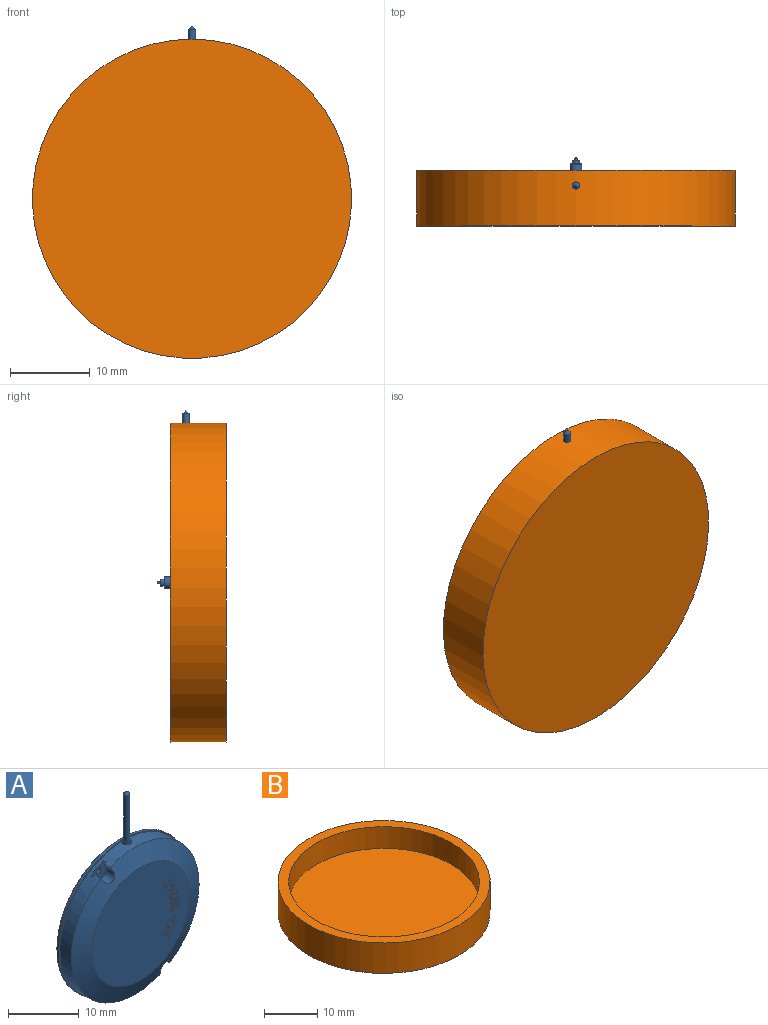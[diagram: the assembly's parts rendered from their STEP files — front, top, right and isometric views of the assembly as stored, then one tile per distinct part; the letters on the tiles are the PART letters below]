
ASSEMBLY  parts=2 mates=1
PART A: 165 faces, bbox 26x6.4x34.7 mm
  f0: cylinder r=0.51mm len=1.05mm, axis (0,-1,0), area 3.4mm2, adj f28,f42,f50
  f1: cylinder r=0.51mm len=1.05mm, axis (0,-1,0), area 3.4mm2, adj f28,f37,f49
  f2: cylinder r=0.4mm len=2.16mm, axis (0,1,0), area 5.1mm2, adj f13,f14,f21,f28,f48
  f3: cylinder r=0.4mm len=2.15mm, axis (0,1,0), area 5.1mm2, adj f13,f14,f21,f28,f47
  f4: cone r=0.45mm half-angle=45deg, axis (0,0,-1), area 0.9mm2, adj f5
  f5: cylinder r=0.45mm len=8.1mm, axis (0,0,-1), area 22.9mm2, adj f4,f35
  f6: cylinder r=0.55mm len=1.1mm, axis (0,0,-1), area 3.8mm2, adj f34,f35
  f7: cylinder r=0.68mm len=1.35mm, axis (0,0,1), area 3.5mm2, adj f15,f19,f27,f34
  f8: cone r=0.72mm half-angle=30deg, axis (0,-1,0), area 0.3mm2, adj f12,f33
  f9: cylinder r=0.45mm len=0.9mm, axis (0,1,0), area 1.1mm2, adj f32,f33
  f10: cylinder r=0.35mm len=0.7mm, axis (0,1,0), area 1.2mm2, adj f31,f32
  f11: cone r=0.13mm half-angle=0.6deg, axis (0,-1,0), area 0.8mm2, adj f30,f31
  f12: cylinder r=0.75mm len=1.5mm, axis (0,1,0), area 4.2mm2, adj f8,f29
  f13: torus R=9mm, axis (0,-1,0), area 224.2mm2, adj f2,f3,f14,f21,f29
  f14: cylinder r=12.57mm len=24.47mm, axis (0,-1,0), area 15.7mm2, adj f2,f3,f13,f28,f50
  f15: cylinder r=13mm len=26mm, axis (0,-1,0), area 32.6mm2, adj f7,f27,f28
  f16: cone r=12.8mm half-angle=70deg, axis (0,1,0), area 219.9mm2, adj f17,f18,f19,f20,f24,f26,f38,f43
  f17: cone r=12.8mm half-angle=70deg, axis (0,1,0), area 0mm2, adj f16,f19,f39
  f18: cylinder r=12.8mm len=1.16mm, axis (0,-1,0), area 0.5mm2, adj f16,f19,f23,f44
  f19: cylinder r=12.8mm len=25.6mm, axis (0,-1,0), area 176mm2, adj f7,f16,f17,f18,f23,f27,f36,f37
  f20: plane 19.6x19.6mm, normal (0,-1,0), area 296.8mm2, adj f16,f51,f52,f53,f54,f55,f56,f57
  f21: cylinder r=12.57mm len=24.47mm, axis (0,-1,0), area 15.7mm2, adj f2,f3,f13,f28,f49
  f22: cylinder r=1.5mm len=2.82mm, axis (0,1,0), area 2.4mm2, adj f23,f42,f45,f46
  f23: plane 3.11x2.74mm, normal (0,1,0), area 2.4mm2, adj f18,f19,f22,f24,f43,f44,f45,f46
  f24: cylinder r=1.05mm len=1.98mm, axis (0,1,0), area 4.6mm2, adj f16,f23,f43,f44
  f25: cylinder r=1.5mm len=2.82mm, axis (0,1,0), area 2.4mm2, adj f36,f37,f40,f41
  f26: cylinder r=1.05mm len=1.98mm, axis (0,1,0), area 5.4mm2, adj f16,f36,f38,f39
  f27: plane 26x26mm, normal (0,-1,0), area 16.1mm2, adj f7,f15,f19
  f28: plane 26x26mm, normal (0,1,0), area 34.5mm2, adj f0,f1,f2,f3,f14,f15,f21
  f29: plane 18.66x18.66mm, normal (0,1,0), area 271.6mm2, adj f12,f13
  f30: plane 0.25x0.25mm, normal (0,1,0), area 0mm2, adj f11
  f31: plane 0.7x0.7mm, normal (0,1,0), area 0.3mm2, adj f10,f11
  f32: plane 0.9x0.9mm, normal (0,1,0), area 0.3mm2, adj f9,f10
  f33: plane 1.43x1.43mm, normal (0,1,0), area 1mm2, adj f8,f9
  f34: plane 1.35x1.35mm, normal (0,0,1), area 0.5mm2, adj f6,f7
  f35: plane 1.1x1.1mm, normal (0,0,1), area 0.3mm2, adj f5,f6
  f36: plane 3.11x2.74mm, normal (0,1,0), area 2.4mm2, adj f19,f25,f26,f38,f39,f40,f41
  f37: plane 3.11x2.74mm, normal (0,-1,0), area 4.7mm2, adj f1,f19,f25,f40,f41
  f38: plane 1.4x0.58mm, normal (0.88,0,0.47), area 0.8mm2, adj f16,f19,f26,f36
  f39: plane 1.4x0.58mm, normal (-0.88,0,-0.47), area 0.8mm2, adj f17,f19,f26,f36
  f40: plane 0.54x0.5mm, normal (-0.88,0,-0.47), area 0.3mm2, adj f19,f25,f36,f37
  f41: plane 0.54x0.5mm, normal (0.88,0,0.47), area 0.3mm2, adj f19,f25,f36,f37
  f42: plane 3.11x2.74mm, normal (0,-1,0), area 4.7mm2, adj f0,f19,f22,f45,f46
  f43: plane 1.4x0.58mm, normal (-0.88,0,-0.47), area 0.8mm2, adj f16,f19,f23,f24
  f44: plane 1.4x0.58mm, normal (0.88,0,0.47), area 0.8mm2, adj f16,f18,f23,f24
  f45: plane 0.54x0.5mm, normal (0.88,0,0.47), area 0.3mm2, adj f19,f22,f23,f42
  f46: plane 0.54x0.5mm, normal (-0.88,0,-0.47), area 0.3mm2, adj f19,f22,f23,f42
  f47: plane 0.8x0.8mm, normal (0,1,0), area 0.5mm2, adj f3
  f48: plane 0.8x0.8mm, normal (0,1,0), area 0.5mm2, adj f2
  f49: plane 1.02x1.02mm, normal (0,-1,0), area 0.8mm2, adj f1,f21
  f50: plane 1.02x1.02mm, normal (0,-1,0), area 0.8mm2, adj f0,f14
  f51: plane 1.15x0.96mm, normal (0.64,0,0.77), area 0.3mm2, adj f20,f52,f62,f63
  f52: plane 0.66x0.55mm, normal (0.77,0,-0.64), area 0.2mm2, adj f20,f51,f53,f63
  f53: plane 0.2x0.11mm, normal (-0.64,0,-0.77), area 0mm2, adj f20,f52,f54,f63
  f54: plane 0.54x0.45mm, normal (-0.77,0,0.64), area 0.1mm2, adj f20,f53,f55,f63
  f55: plane 0.36x0.3mm, normal (-0.64,0,-0.77), area 0.1mm2, adj f20,f54,f56,f63
  f56: plane 0.54x0.45mm, normal (0.77,0,-0.64), area 0.1mm2, adj f20,f55,f57,f63
  f57: plane 0.2x0.11mm, normal (-0.64,0,-0.77), area 0mm2, adj f20,f56,f58,f63
  f58: plane 0.54x0.45mm, normal (-0.77,0,0.64), area 0.1mm2, adj f20,f57,f59,f63
  f59: plane 0.45x0.37mm, normal (-0.64,0,-0.77), area 0.1mm2, adj f20,f58,f60,f63
  f60: plane 0.54x0.45mm, normal (0.77,0,-0.64), area 0.1mm2, adj f20,f59,f61,f63
  f61: plane 0.2x0.11mm, normal (-0.64,0,-0.77), area 0mm2, adj f20,f60,f62,f63
  f62: plane 0.65x0.54mm, normal (-0.77,0,0.64), area 0.2mm2, adj f20,f51,f61,f63
  f63: plane 1.69x1.61mm, normal (0,-1,0), area 0.5mm2, adj f51,f52,f53,f54,f55,f56,f57,f58
  f64: plane 0.2x0.1mm, normal (-0.54,0,0.84), area 0mm2, adj f20,f65,f67,f68
  f65: plane 0.47x0.3mm, normal (0.84,0,0.54), area 0.1mm2, adj f20,f64,f66,f68
  f66: plane 0.2x0.1mm, normal (0.54,0,-0.84), area 0mm2, adj f20,f65,f67,f68
  f67: plane 0.47x0.3mm, normal (-0.84,0,-0.54), area 0.1mm2, adj f20,f64,f66,f68
  f68: plane 0.54x0.41mm, normal (0,-1,0), area 0.1mm2, adj f64,f65,f66,f67
  f69: extruded ~0.5x0.2mm, area 0.1mm2, adj f20,f70,f80,f81
  f70: plane 0.2x0.11mm, normal (-0.77,0,-0.64), area 0mm2, adj f20,f69,f71,f81
  f71: extruded ~0.71x0.2mm, area 0.2mm2, adj f20,f70,f72,f81
  f72: extruded ~0.64x0.2mm, area 0.1mm2, adj f20,f71,f73,f81
  f73: extruded ~0.61x0.2mm, area 0.1mm2, adj f20,f72,f74,f81
  f74: plane 0.55x0.2mm, normal (-0.05,0,-1), area 0.1mm2, adj f20,f73,f75,f81
  f75: plane 0.53x0.44mm, normal (0.77,0,0.64), area 0.1mm2, adj f20,f74,f76,f81
  f76: plane 0.2x0.11mm, normal (0.64,0,-0.77), area 0mm2, adj f20,f75,f77,f81
  f77: plane 0.78x0.65mm, normal (-0.77,0,-0.64), area 0.2mm2, adj f20,f76,f78,f81
  f78: plane 0.84x0.2mm, normal (0.05,0,1), area 0.2mm2, adj f20,f77,f79,f81
  f79: extruded ~0.54x0.2mm, area 0.1mm2, adj f20,f78,f80,f81
  f80: extruded ~0.45x0.2mm, area 0.1mm2, adj f20,f69,f79,f81
  f81: plane 1.63x1.53mm, normal (0,-1,0), area 0.5mm2, adj f69,f70,f71,f72,f73,f74,f75,f76
  f82: plane 1.43x0.28mm, normal (0.19,0,0.98), area 0.3mm2, adj f20,f83,f91,f92
  f83: plane 0.2x0.03mm, normal (0.91,0,0.41), area 0mm2, adj f20,f82,f84,f92
  f84: plane 0.95x0.43mm, normal (0.41,0,-0.91), area 0.2mm2, adj f20,f83,f85,f92
  f85: plane 0.2x0.17mm, normal (0.91,0,0.41), area 0mm2, adj f20,f84,f86,f92
  f86: plane 0.2x0.13mm, normal (0.41,0,-0.91), area 0mm2, adj f20,f85,f87,f92
  f87: plane 0.2x0.17mm, normal (-0.91,0,-0.41), area 0mm2, adj f20,f86,f88,f92
  f88: plane 0.32x0.2mm, normal (0.41,0,-0.91), area 0.1mm2, adj f20,f87,f89,f92
  f89: plane 0.2x0.14mm, normal (-0.91,0,-0.41), area 0mm2, adj f20,f88,f90,f92
  f90: plane 0.32x0.2mm, normal (-0.41,0,0.91), area 0.1mm2, adj f20,f89,f91,f92
  f91: plane 0.65x0.29mm, normal (-0.91,0,-0.41), area 0.1mm2, adj f20,f82,f90,f92
  f92: plane 1.46x0.96mm, normal (0,-1,0), area 0.5mm2, adj f82,f83,f84,f85,f86,f87,f88,f89
  f93: plane 0.4x0.2mm, normal (0.91,0,0.41), area 0.1mm2, adj f92,f94,f95,f162
  f94: plane 0.75x0.2mm, normal (-0.19,0,-0.98), area 0.2mm2, adj f92,f93,f95,f162
  f95: plane 0.57x0.26mm, normal (-0.41,0,0.91), area 0.1mm2, adj f92,f93,f94,f162
  f96: extruded ~0.44x0.25mm, area 0.1mm2, adj f20,f97,f107,f108
  f97: plane 0.2x0.14mm, normal (-0.97,0,-0.25), area 0mm2, adj f20,f96,f98,f108
  f98: extruded ~0.62x0.37mm, area 0.2mm2, adj f20,f97,f99,f108
  f99: extruded ~0.56x0.34mm, area 0.1mm2, adj f20,f98,f100,f108
  f100: extruded ~0.6x0.2mm, area 0.1mm2, adj f20,f99,f101,f108
  f101: plane 0.48x0.26mm, normal (-0.47,0,-0.88), area 0.1mm2, adj f20,f100,f102,f108
  f102: plane 0.67x0.2mm, normal (0.97,0,0.25), area 0.1mm2, adj f20,f101,f103,f108
  f103: plane 0.2x0.14mm, normal (0.25,0,-0.97), area 0mm2, adj f20,f102,f104,f108
  f104: plane 0.99x0.25mm, normal (-0.97,0,-0.25), area 0.2mm2, adj f20,f103,f105,f108
  f105: plane 0.74x0.4mm, normal (0.47,0,0.88), area 0.2mm2, adj f20,f104,f106,f108
  f106: extruded ~0.52x0.2mm, area 0.1mm2, adj f20,f105,f107,f108
  f107: extruded ~0.39x0.23mm, area 0.1mm2, adj f20,f96,f106,f108
  f108: plane 1.64x1.22mm, normal (0,-1,0), area 0.5mm2, adj f96,f97,f98,f99,f100,f101,f102,f103
  f109: extruded ~0.33x0.2mm, area 0.1mm2, adj f20,f110,f117,f118
  f110: extruded ~0.37x0.31mm, area 0.1mm2, adj f20,f109,f111,f118
  f111: extruded ~0.31x0.2mm, area 0.1mm2, adj f20,f110,f112,f118
  f112: extruded ~0.38x0.2mm, area 0.1mm2, adj f20,f111,f113,f118
  f113: extruded ~0.53x0.42mm, area 0.2mm2, adj f20,f112,f114,f118
  f114: extruded ~0.42x0.26mm, area 0.1mm2, adj f20,f113,f115,f118
  f115: extruded ~0.31x0.24mm, area 0.1mm2, adj f20,f114,f116,f118
  f116: extruded ~0.42x0.42mm, area 0.1mm2, adj f20,f115,f117,f118
  f117: extruded ~0.45x0.37mm, area 0.1mm2, adj f20,f109,f116,f118
  f118: plane 1.57x1.01mm, normal (0,-1,0), area 0.6mm2, adj f109,f110,f111,f112,f113,f114,f115,f116
  f119: extruded ~0.3x0.22mm, area 0.1mm2, adj f118,f120,f122,f127
  f120: extruded ~0.28x0.26mm, area 0.1mm2, adj f118,f119,f121,f127
  f121: extruded ~0.31x0.24mm, area 0.1mm2, adj f118,f120,f122,f127
  f122: extruded ~0.27x0.27mm, area 0.1mm2, adj f118,f119,f121,f127
  f123: extruded ~0.37x0.3mm, area 0.1mm2, adj f118,f124,f126,f163
  f124: extruded ~0.35x0.33mm, area 0.1mm2, adj f118,f123,f125,f163
  f125: extruded ~0.38x0.28mm, area 0.1mm2, adj f118,f124,f126,f163
  f126: extruded ~0.36x0.34mm, area 0.1mm2, adj f118,f123,f125,f163
  f127: plane 0.57x0.51mm, normal (0,-1,0), area 0.2mm2, adj f119,f120,f121,f122
  f128: extruded ~0.38x0.33mm, area 0.1mm2, adj f20,f129,f139,f140
  f129: plane 0.2x0.14mm, normal (-1,0,0.1), area 0mm2, adj f20,f128,f130,f140
  f130: extruded ~0.54x0.45mm, area 0.2mm2, adj f20,f129,f131,f140
  f131: extruded ~0.49x0.41mm, area 0.1mm2, adj f20,f130,f132,f140
  f132: extruded ~0.5x0.35mm, area 0.1mm2, adj f20,f131,f133,f140
  f133: plane 0.41x0.36mm, normal (-0.75,0,-0.66), area 0.1mm2, adj f20,f132,f134,f140
  f134: plane 0.68x0.2mm, normal (0.99,0,-0.1), area 0.1mm2, adj f20,f133,f135,f140
  f135: plane 0.2x0.14mm, normal (-0.1,0,-0.99), area 0mm2, adj f20,f134,f136,f140
  f136: plane 1x0.2mm, normal (-0.99,0,0.1), area 0.2mm2, adj f20,f135,f137,f140
  f137: plane 0.63x0.55mm, normal (0.75,0,0.66), area 0.2mm2, adj f20,f136,f138,f140
  f138: extruded ~0.43x0.32mm, area 0.1mm2, adj f20,f137,f139,f140
  f139: extruded ~0.34x0.29mm, area 0.1mm2, adj f20,f128,f138,f140
  f140: plane 1.57x1.1mm, normal (0,-1,0), area 0.5mm2, adj f128,f129,f130,f131,f132,f133,f134,f135
  f141: plane 0.28x0.2mm, normal (-0.84,0,0.53), area 0.1mm2, adj f20,f142,f148,f149
  f142: plane 0.2x0.12mm, normal (0.53,0,0.85), area 0mm2, adj f20,f141,f143,f149
  f143: plane 0.69x0.44mm, normal (0.85,0,-0.53), area 0.2mm2, adj f20,f142,f144,f149
  f144: plane 0.2x0.12mm, normal (-0.53,0,-0.85), area 0mm2, adj f20,f143,f145,f149
  f145: plane 0.28x0.2mm, normal (-0.85,0,0.53), area 0.1mm2, adj f20,f144,f146,f149
  f146: plane 1.14x0.72mm, normal (-0.53,0,-0.85), area 0.3mm2, adj f20,f145,f147,f149
  f147: plane 0.2x0.13mm, normal (-0.85,0,0.53), area 0mm2, adj f20,f146,f148,f149
  f148: plane 1.14x0.72mm, normal (0.53,0,0.85), area 0.3mm2, adj f20,f141,f147,f149
  f149: plane 1.52x1.2mm, normal (0,-1,0), area 0.3mm2, adj f141,f142,f143,f144,f145,f146,f147,f148
  f150: plane 0.2x0.03mm, normal (0.93,0,-0.38), area 0mm2, adj f20,f151,f157,f158
  f151: plane 1.64x0.2mm, normal (0.05,0,-1), area 0.3mm2, adj f20,f150,f152,f158
  f152: plane 0.2x0.15mm, normal (-0.93,0,0.38), area 0mm2, adj f20,f151,f153,f158
  f153: plane 0.54x0.2mm, normal (-0.06,0,1), area 0.1mm2, adj f20,f152,f154,f158
  f154: plane 0.6x0.24mm, normal (-0.93,0,0.38), area 0.1mm2, adj f20,f153,f155,f158
  f155: plane 0.4x0.37mm, normal (-0.74,0,-0.67), area 0.1mm2, adj f20,f154,f156,f158
  f156: plane 0.2x0.15mm, normal (-0.93,0,0.38), area 0mm2, adj f20,f155,f157,f158
  f157: plane 1.22x1.11mm, normal (0.74,0,0.68), area 0.3mm2, adj f20,f150,f156,f158
  f158: plane 1.66x1.33mm, normal (0,-1,0), area 0.5mm2, adj f150,f151,f152,f153,f154,f155,f156,f157
  f159: plane 0.6x0.2mm, normal (-0.05,0,1), area 0.1mm2, adj f158,f160,f161,f164
  f160: plane 0.47x0.2mm, normal (0.93,0,-0.38), area 0.1mm2, adj f158,f159,f161,f164
  f161: plane 0.44x0.4mm, normal (-0.74,0,-0.67), area 0.1mm2, adj f158,f159,f160,f164
  f162: plane 0.75x0.4mm, normal (0,-1,0), area 0.1mm2, adj f93,f94,f95
  f163: plane 0.71x0.64mm, normal (0,-1,0), area 0.4mm2, adj f123,f124,f125,f126
  f164: plane 0.6x0.47mm, normal (0,-1,0), area 0.1mm2, adj f159,f160,f161
PART B: 5 faces, bbox 40x40x7 mm
  f0: plane 36x36mm, normal (0,0,1), area 1017.9mm2, adj f1
  f1: cylinder r=18mm len=36mm, axis (0,0,1), area 565.5mm2, adj f0,f2
  f2: plane 40x40mm, normal (0,0,1), area 238.8mm2, adj f1,f3
  f3: cylinder r=20mm len=40mm, axis (0,0,1), area 879.6mm2, adj f2,f4
  f4: plane 40x40mm, normal (0,0,-1), area 1256.6mm2, adj f3
PLACE A t=(-0.1,-0.5,0)mm
PLACE B rot(axis=(-0.58,-0.58,-0.58),120deg) t=(-0.1,4.25,0)mm
MATE revolute B.f1 <-> A.f8  axis (0,1,0) through (-0.1,1.75,0)mm
